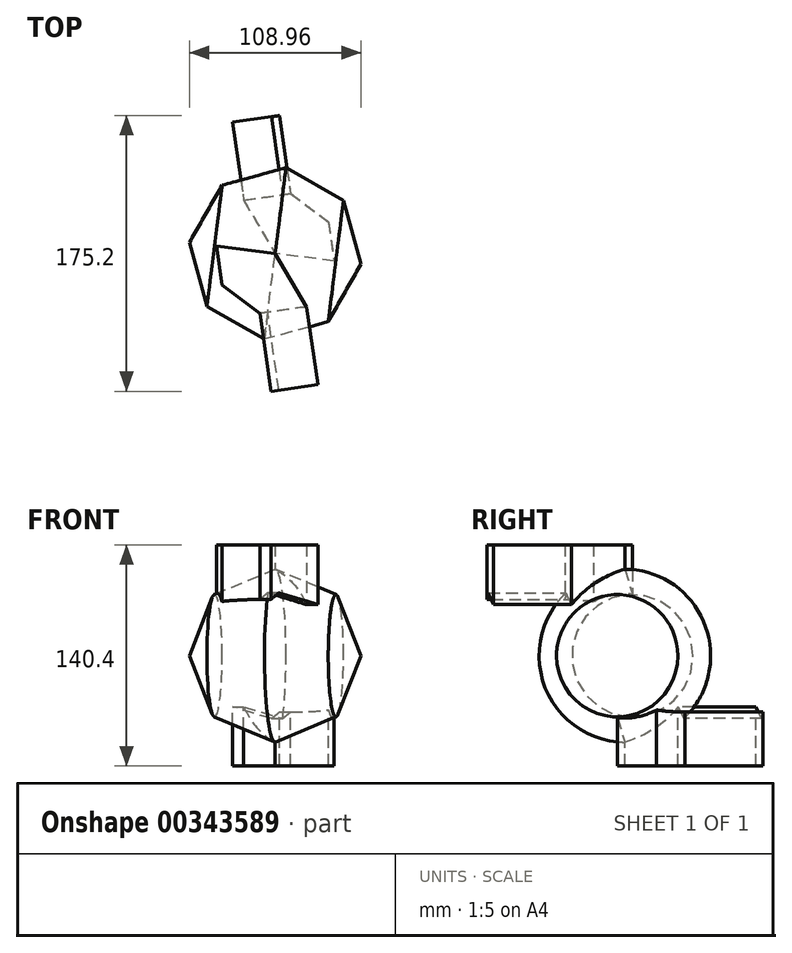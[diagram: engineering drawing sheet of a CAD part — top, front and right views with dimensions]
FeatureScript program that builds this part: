
annotation { "Feature Type Name" : "Feature", "Feature Type Description" : "" }
export const myFeature = defineFeature(function(context is Context, id is Id, definition is map)
    precondition{}
    {
        {
            var Q0;
            Q0=qCreatedBy(makeId("Top.planeOp"),FACE);
            var sketch = newSketch(context, id + "F0", { "sketchPlane" : qUnion([Q0])});
            skCircle(sketch, "E0.cCircle", {"center": v(0, 0) * mm, "radius": 50.73 * mm, "construction": true});
            skLineSegment(sketch, "E0.0", {"start": v(-54.48, 6.85) * mm, "end": v(-33.68, 43.37) * mm});
            skLineSegment(sketch, "E0.1", {"start": v(-33.68, 43.37) * mm, "end": v(6.85, 54.48) * mm});
            skLineSegment(sketch, "E0.2", {"start": v(6.85, 54.48) * mm, "end": v(43.37, 33.68) * mm});
            skLineSegment(sketch, "E0.3", {"start": v(43.37, 33.68) * mm, "end": v(54.48, -6.85) * mm});
            skLineSegment(sketch, "E0.4", {"start": v(54.48, -6.85) * mm, "end": v(33.68, -43.37) * mm});
            skLineSegment(sketch, "E0.5", {"start": v(33.68, -43.37) * mm, "end": v(-6.85, -54.48) * mm});
            skLineSegment(sketch, "E0.6", {"start": v(-6.85, -54.48) * mm, "end": v(-43.37, -33.68) * mm});
            skLineSegment(sketch, "E0.7", {"start": v(-43.37, -33.68) * mm, "end": v(-54.48, 6.85) * mm});
            skPoint(sketch, "E0.0.midPoint", {"position": v(-44.08, 25.1) * mm});
            skLineSegment(sketch, "E1", {"start": v(54.48, -6.85) * mm, "end": v(-54.48, 6.85) * mm});
            skSolve(sketch);
        }
        {
            var Q0;
            Q0=makeQuery(id+"F0.imprint","IMPRINT",FACE,{"disambiguationData":[TD([[makeQuery(id+"F0.imprint","IMPRINT",EDGE,{"derivedFrom":sQuery(id+"F0.wireOp",EDGE,"E0.0")}),-1.0]])]});
            var sketch = newSketch(context, id + "F1", { "sketchPlane" : qUnion([Q0])});
            skCircle(sketch, "E2.cCircle", {"center": v(0, 0) * mm, "radius": 36.34 * mm, "construction": true});
            skLineSegment(sketch, "E2.0", {"start": v(38.1, -9.8) * mm, "end": v(20.01, -33.86) * mm});
            skLineSegment(sketch, "E2.1", {"start": v(20.01, -33.86) * mm, "end": v(-9.8, -38.1) * mm});
            skLineSegment(sketch, "E2.2", {"start": v(-9.8, -38.1) * mm, "end": v(-33.86, -20.01) * mm});
            skLineSegment(sketch, "E2.3", {"start": v(-33.86, -20.01) * mm, "end": v(-38.1, 9.8) * mm});
            skLineSegment(sketch, "E2.4", {"start": v(-38.1, 9.8) * mm, "end": v(-20.01, 33.86) * mm});
            skLineSegment(sketch, "E2.5", {"start": v(-20.01, 33.86) * mm, "end": v(9.8, 38.1) * mm});
            skLineSegment(sketch, "E2.6", {"start": v(9.8, 38.1) * mm, "end": v(33.86, 20.01) * mm});
            skLineSegment(sketch, "E2.7", {"start": v(33.86, 20.01) * mm, "end": v(38.1, -9.8) * mm});
            skPoint(sketch, "E2.0.midPoint", {"position": v(29.05, -21.83) * mm});
            skLineSegment(sketch, "E3", {"start": v(-20.01, 33.86) * mm, "end": v(20.01, -33.86) * mm});
            skSolve(sketch);
        }
        {
            var Q0;
            Q0=makeQuery(id+"F0.imprint","IMPRINT",FACE,{"disambiguationData":[TD([[makeQuery(id+"F0.imprint","IMPRINT",EDGE,{"derivedFrom":sQuery(id+"F0.wireOp",EDGE,"E0.0")}),-1.0]])]});
            var Q1;
            Q1=sQuery(id+"F0.wireOp",EDGE,"E1");
            revolve(context, id + "F2", {"entities" : qUnion([Q0]), "axis" : qUnion([Q1]), "revolveType" : RevolveType.FULL});
        }
        {
            var Q0;
            {var subQ5=sQuery(id+"F1.wireOp",EDGE,"E2.1");Q0=makeQuery(id+"F1.imprint","IMPRINT",FACE,{"disambiguationData":[TD([[makeQuery(id+"F1.imprint","IMPRINT",EDGE,{"derivedFrom":subQ5}),-1.0]])]});}
            extrude(context, id + "F3", {"entities" : qUnion([Q0]), "operationType" : NewBodyOperationType.ADD, "depth" : 70.4 * mm});
        }
        {
            var Q0;
            {var subQ1=sQuery(id+"F1.wireOp",EDGE,"E2.5");Q0=makeQuery(id+"F1.imprint","IMPRINT",FACE,{"disambiguationData":[TD([[makeQuery(id+"F1.imprint","IMPRINT",EDGE,{"derivedFrom":subQ1}),-1.0]])]});}
            extrude(context, id + "F4", {"entities" : qUnion([Q0]), "operationType" : NewBodyOperationType.ADD, "oppositeDirection" : true, "depth" : 70 * mm});
        }
        {
            var Q0;
            Q0=makeQuery(id+"F3.opExtrude","SWEPT_FACE",FACE,{"disambiguationData":[OSD([sQuery(id+"F1.wireOp",EDGE,"E2.1")])]});
            extrude(context, id + "F5", {"entities" : qUnion([Q0]), "operationType" : NewBodyOperationType.ADD, "depth" : 50 * mm});
        }
        {
            var Q0;
            Q0=makeQuery(id+"F4.opExtrude","SWEPT_FACE",FACE,{"disambiguationData":[OSD([sQuery(id+"F1.wireOp",EDGE,"E2.5")])]});
            extrude(context, id + "F6", {"entities" : qUnion([Q0]), "operationType" : NewBodyOperationType.ADD, "depth" : 50 * mm});
        }
    });
